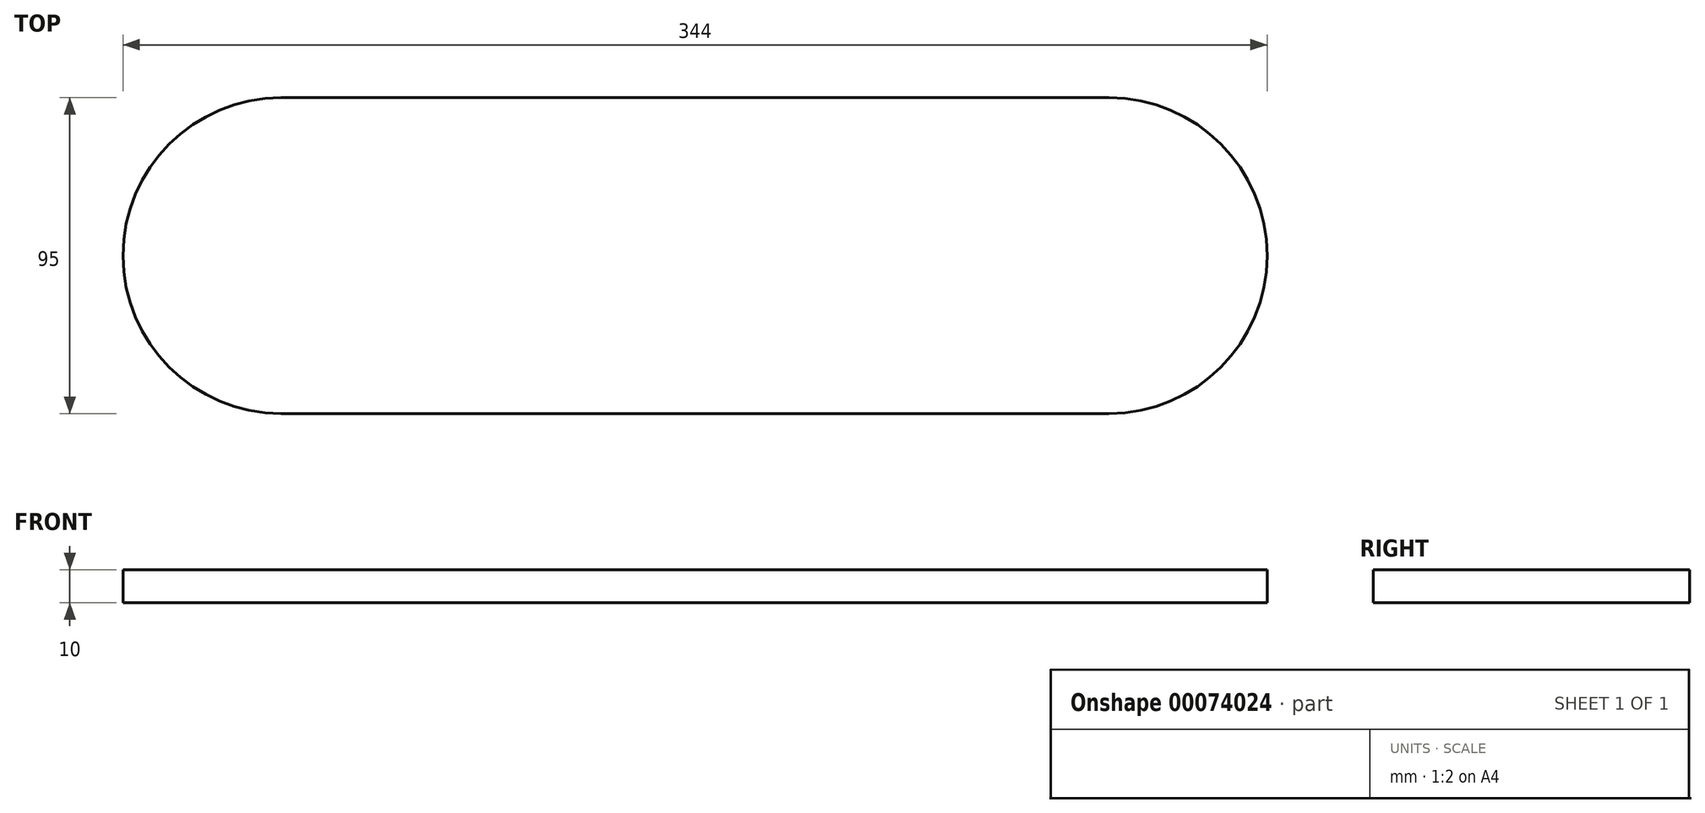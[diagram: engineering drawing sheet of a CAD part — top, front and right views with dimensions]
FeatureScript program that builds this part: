
annotation { "Feature Type Name" : "Feature", "Feature Type Description" : "" }
export const myFeature = defineFeature(function(context is Context, id is Id, definition is map)
    precondition{}
    {
        {
            var Q0;
            Q0=qCreatedBy(makeId("Top.planeOp"),FACE);
            var sketch = newSketch(context, id + "F0", { "sketchPlane" : qUnion([Q0])});
            skArc(sketch, "E0", {"start": v(0, 47.5) * mm, "mid": v(-47.5, 0) * mm, "end": v(0, -47.5) * mm});
            skArc(sketch, "E1", {"start": v(249, -47.5) * mm, "mid": v(296.5, 0) * mm, "end": v(249, 47.5) * mm});
            skPoint(sketch, "E2", {"position": v(-47.5, 0) * mm});
            skPoint(sketch, "E3", {"position": v(296.5, 0) * mm});
            skLineSegment(sketch, "E4", {"start": v(0, -47.5) * mm, "end": v(249, -47.5) * mm});
            skLineSegment(sketch, "E5", {"start": v(0, 47.5) * mm, "end": v(249, 47.5) * mm});
            skSolve(sketch);
        }
        {
            var Q0;
            Q0=makeQuery(id+"F0.imprint","IMPRINT",FACE,{"disambiguationData":[TD([[makeQuery(id+"F0.imprint","IMPRINT",EDGE,{"derivedFrom":sQuery(id+"F0.wireOp",EDGE,"E0")}),1.0]])]});
            extrude(context, id + "F1", {"entities" : qUnion([Q0]), "depth" : 10 * mm, "offsetDistance" : 25 * mm});
        }
    });
